# Revit family: LOROWERK 01111-050X
name_source: partatom
category: Rohrformteile
revit_build: Autodesk Revit 2017 (Build: 20160225_1515(x64)
units: mm (PartAtom-declared; Revit-internal decimal feet)

## family parameters
Arbeitsebenenbasiert = Nein
Beim Laden mit Abzugskörper schneiden = Nein
Bemaßung runder Anschluss = Durchmesser verwenden
Gemeinsam genutzt = Nein
Immer vertikal = Ja
Teiletyp = Unterbricht

## types (1)
- LOROWERK 01111-050X
    Außendurchmesser Rohr [mm] = 53
    Beschreibung = LORO-X Stahlabflussrohre
    Brandschutzklasse = B1 nach DIN 4102
    CONNECTOR0_DIAMETER_dZ_0r = 50 mm
    CONNECTOR0_dZ_00 = 1497 mm
    CONNECTOR0_dZ_01 = 1538 mm
    CONNECTOR0_ref_dZ = 1497 mm
    CONNECTOR1_DIAMETER_dZ_0r = 50 mm
    CONNECTOR1_dZ_01 = 41 mm
    CONNECTOR1_ref_dZ = 41 mm
    DATANORM = 01111.050X
    GTIN = 4038088005897
    HAN = 01111.050X
    HeinzeBIM = https://www.heinze.de
    Hersteller = LOROWERK K.H. Vahlbrauk GmbH & Co. KG
    Index = 20
    Index Number = 5
    Lieferform = Stück
    Lieferlänge [m] = 1.5
    Nenndruck Text = 0.5
    Nenndrucksystem Text = PN
    Nennmaß Text = 50
    Nennweitensystem Text = DN
    Normen/Regeln/Zulassungen = DVGW für Trinkwasser
    Nutzbare Rohrlänge [m] = 1.5
    Produktbezeichnung Text = LORO-X Stahlabflussrohre
    Produktkennung = Rohr
    Produktname Text = LORO-X Rohre mit einer Muffe
    Querschnittsform = rund
    Rohrgewicht pro Meter (leer) [kg/m] = 2
    Typname = LORO-X Rohre mit einer Muffe
    VDIBSN = 020001???001001???00100100000100300700000000000001000000010000500000
    Verbindungsart I = Pressen
    Verbindungsart II = axial pressen
    Verlegeart = Unterputz
    Wanddicke [mm] = 1.5
    Wärmeausdehnungskoeffizient Rohr [mm/(m.K)] = 0.0117
    max. zul. Dauer-Betriebstemperatur [°C] = 95
